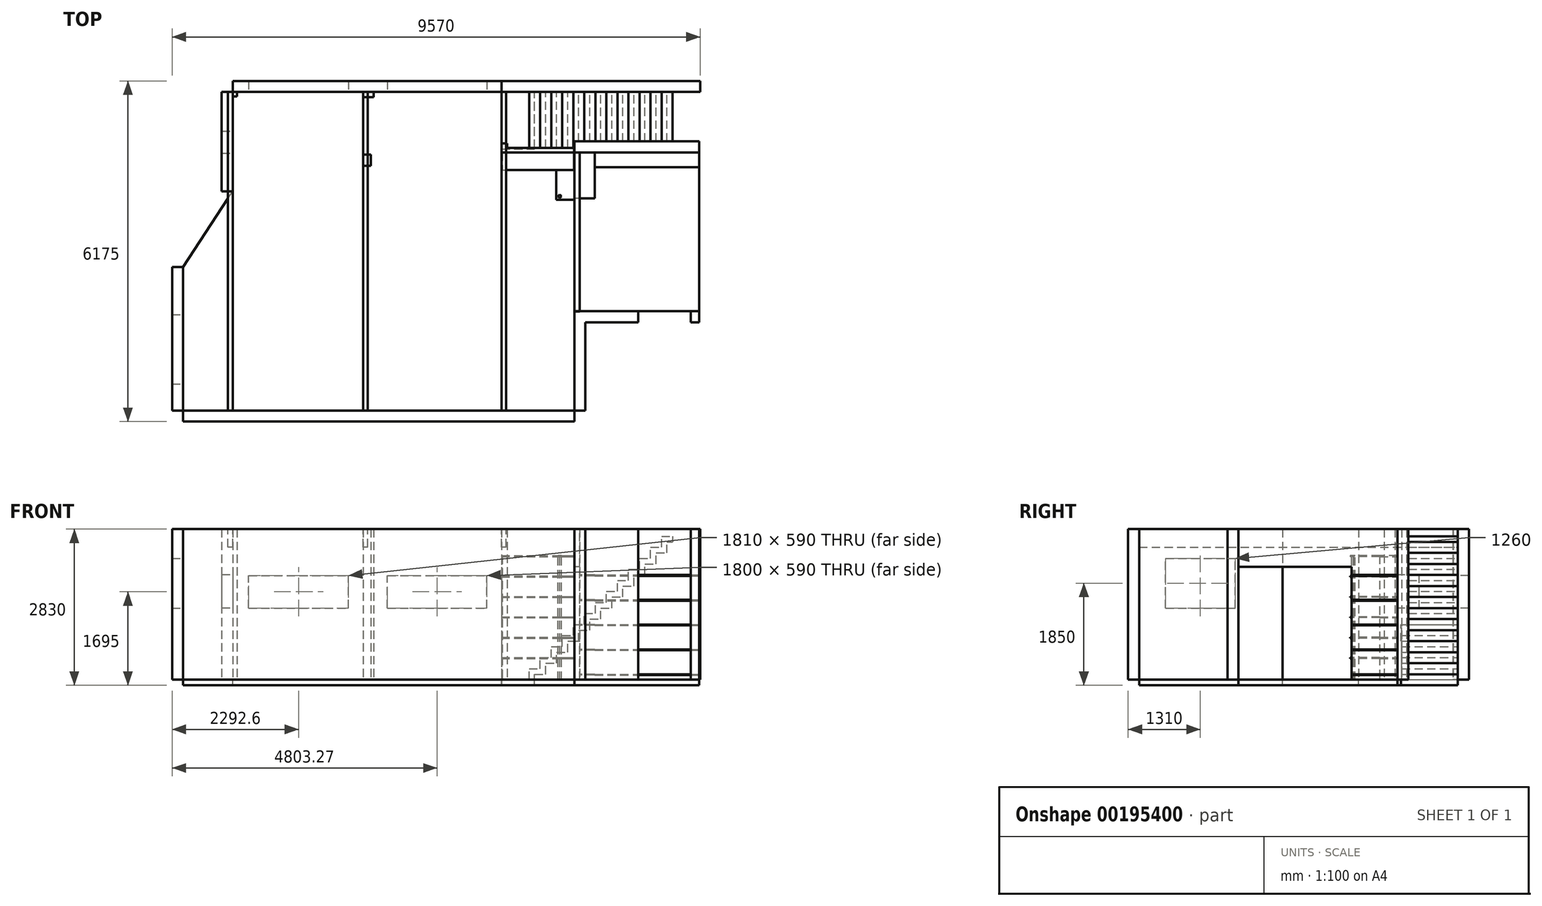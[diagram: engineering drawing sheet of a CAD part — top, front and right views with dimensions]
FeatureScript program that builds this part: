
annotation { "Feature Type Name" : "Feature", "Feature Type Description" : "" }
export const myFeature = defineFeature(function(context is Context, id is Id, definition is map)
    precondition{}
    {
        {
            var Q0;
            Q0=qCreatedBy(makeId("Top.planeOp"),FACE);
            var sketch = newSketch(context, id + "F0", { "sketchPlane" : qUnion([Q0])});
            skLineSegment(sketch, "E0.bottom", {"start": v(0, 0) * mm, "end": v(7090, 0) * mm});
            skLineSegment(sketch, "E0.top", {"start": v(0, 5775) * mm, "end": v(7090, 5775) * mm});
            skLineSegment(sketch, "E0.left", {"start": v(0, 0) * mm, "end": v(0, 5775) * mm});
            skLineSegment(sketch, "E0.right", {"start": v(7090, 0) * mm, "end": v(7090, 5775) * mm});
            skLineSegment(sketch, "E1", {"start": v(7090, 0) * mm, "end": v(7090, 1800) * mm, "construction": true});
            skLineSegment(sketch, "E2.bottom", {"start": v(7090, 1800) * mm, "end": v(9350, 1800) * mm});
            skLineSegment(sketch, "E2.top", {"start": v(7090, 4680) * mm, "end": v(9350, 4680) * mm});
            skLineSegment(sketch, "E2.left", {"start": v(7090, 1800) * mm, "end": v(7090, 4680) * mm});
            skLineSegment(sketch, "E2.right", {"start": v(9350, 1800) * mm, "end": v(9350, 4680) * mm});
            skLineSegment(sketch, "E3", {"start": v(7090, 4680) * mm, "end": v(7090, 3850) * mm, "construction": true});
            skLineSegment(sketch, "E4", {"start": v(0, 5775) * mm, "end": v(900, 5775) * mm, "construction": true});
            skLineSegment(sketch, "E5", {"start": v(900, 5775) * mm, "end": v(900, 3975) * mm, "construction": true});
            skLineSegment(sketch, "E6", {"start": v(0, 0) * mm, "end": v(0, 2600) * mm, "construction": true});
            skLineSegment(sketch, "E7", {"start": v(0, 2600) * mm, "end": v(900, 3975) * mm, "construction": true});
            skSolve(sketch);
        }
        {
            var Q0;
            Q0 = qSketchRegion(id + "F0", true);
            extrude(context, id + "F1", {"entities" : qUnion([Q0]), "oppositeDirection" : true, "depth" : 100 * mm});
        }
        {
            var Q0;
            Q0=makeQuery(id+"F1.opExtrude","CAP_FACE",FACE,{"disambiguationData":[OSD([sQuery(id+"F0.wireOp",EDGE,"E0.bottom"),sQuery(id+"F0.wireOp",EDGE,"E0.top"),sQuery(id+"F0.wireOp",EDGE,"E0.left"),sQuery(id+"F0.wireOp",EDGE,"E0.right"),sQuery(id+"F0.wireOp",EDGE,"E2.bottom"),sQuery(id+"F0.wireOp",EDGE,"E2.top"),sQuery(id+"F0.wireOp",EDGE,"E2.right")])],"isStart":true});
            var sketch = newSketch(context, id + "F2", { "sketchPlane" : qUnion([Q0])});
            skLineSegment(sketch, "E8", {"start": v(0, 5775) * mm, "end": v(900, 5775) * mm});
            skLineSegment(sketch, "E9", {"start": v(900, 5775) * mm, "end": v(900, 3975) * mm});
            skLineSegment(sketch, "E10", {"start": v(0, 2600) * mm, "end": v(900, 3975) * mm});
            skLineSegment(sketch, "E11", {"start": v(0, 5775) * mm, "end": v(0, 2600) * mm});
            skSolve(sketch);
        }
        {
            var Q0;
            Q0 = qSketchRegion(id + "F2", true);
            extrude(context, id + "F3", {"entities" : qUnion([Q0]), "operationType" : NewBodyOperationType.REMOVE, "endBound" : BoundingType.SYMMETRIC, "oppositeDirection" : true, "depth" : 210 * mm});
        }
        {
            var Q0;
            Q0=makeQuery(id+"F1.opExtrude","CAP_FACE",FACE,{"disambiguationData":[OSD([sQuery(id+"F0.wireOp",EDGE,"E0.bottom"),sQuery(id+"F0.wireOp",EDGE,"E0.top"),sQuery(id+"F0.wireOp",EDGE,"E0.left"),sQuery(id+"F0.wireOp",EDGE,"E0.right"),sQuery(id+"F0.wireOp",EDGE,"E2.bottom"),sQuery(id+"F0.wireOp",EDGE,"E2.top"),sQuery(id+"F0.wireOp",EDGE,"E2.right")])],"isStart":true});
            var sketch = newSketch(context, id + "F4", { "sketchPlane" : qUnion([Q0])});
            skLineSegment(sketch, "E12.bottom", {"start": v(0, 0) * mm, "end": v(-200, 0) * mm});
            skLineSegment(sketch, "E12.top", {"start": v(0, 2600) * mm, "end": v(-200, 2600) * mm});
            skLineSegment(sketch, "E12.left", {"start": v(0, 0) * mm, "end": v(0, 2600) * mm});
            skLineSegment(sketch, "E12.right", {"start": v(-200, 0) * mm, "end": v(-200, 2600) * mm});
            skLineSegment(sketch, "E13.bottom", {"start": v(900, 5775) * mm, "end": v(700, 5775) * mm});
            skLineSegment(sketch, "E13.top", {"start": v(900, 3975) * mm, "end": v(700, 3975) * mm});
            skLineSegment(sketch, "E13.left", {"start": v(900, 5775) * mm, "end": v(900, 3975) * mm});
            skLineSegment(sketch, "E13.right", {"start": v(700, 5775) * mm, "end": v(700, 3975) * mm});
            skLineSegment(sketch, "E14.bottom", {"start": v(900, 5775) * mm, "end": v(7090, 5775) * mm});
            skLineSegment(sketch, "E14.top", {"start": v(900, 5975) * mm, "end": v(7090, 5975) * mm});
            skLineSegment(sketch, "E14.left", {"start": v(900, 5775) * mm, "end": v(900, 5975) * mm});
            skLineSegment(sketch, "E14.right", {"start": v(7090, 5775) * mm, "end": v(7090, 5975) * mm});
            skLineSegment(sketch, "E15.bottom", {"start": v(0, 0) * mm, "end": v(7090, 0) * mm});
            skLineSegment(sketch, "E15.top", {"start": v(0, -200) * mm, "end": v(7090, -200) * mm});
            skLineSegment(sketch, "E15.left", {"start": v(0, 0) * mm, "end": v(0, -200) * mm});
            skLineSegment(sketch, "E15.right", {"start": v(7090, 0) * mm, "end": v(7090, -200) * mm});
            skLineSegment(sketch, "E16.bottom", {"start": v(7090, 0) * mm, "end": v(7290, 0) * mm});
            skLineSegment(sketch, "E16.top", {"start": v(7090, 1800) * mm, "end": v(7290, 1800) * mm});
            skLineSegment(sketch, "E16.left", {"start": v(7090, 0) * mm, "end": v(7090, 1800) * mm});
            skLineSegment(sketch, "E16.right", {"start": v(7290, 0) * mm, "end": v(7290, 1800) * mm});
            skLineSegment(sketch, "E17.bottom", {"start": v(7090, 1800) * mm, "end": v(8250, 1800) * mm});
            skLineSegment(sketch, "E17.top", {"start": v(7090, 1600) * mm, "end": v(8250, 1600) * mm});
            skLineSegment(sketch, "E17.left", {"start": v(7090, 1800) * mm, "end": v(7090, 1600) * mm});
            skLineSegment(sketch, "E17.right", {"start": v(8250, 1800) * mm, "end": v(8250, 1600) * mm});
            skLineSegment(sketch, "E18.bottom", {"start": v(9350, 1800) * mm, "end": v(9200, 1800) * mm});
            skLineSegment(sketch, "E18.top", {"start": v(9350, 1600) * mm, "end": v(9200, 1600) * mm});
            skLineSegment(sketch, "E18.left", {"start": v(9350, 1800) * mm, "end": v(9350, 1600) * mm});
            skLineSegment(sketch, "E18.right", {"start": v(9200, 1800) * mm, "end": v(9200, 1600) * mm});
            skLineSegment(sketch, "E19.bottom", {"start": v(7090, 4680) * mm, "end": v(9350, 4680) * mm});
            skLineSegment(sketch, "E19.top", {"start": v(7090, 4880) * mm, "end": v(9350, 4880) * mm});
            skLineSegment(sketch, "E19.left", {"start": v(7090, 4680) * mm, "end": v(7090, 4880) * mm});
            skLineSegment(sketch, "E19.right", {"start": v(9350, 4680) * mm, "end": v(9350, 4880) * mm});
            skSolve(sketch);
        }
        {
            var Q0;
            Q0 = qSketchRegion(id + "F4", true);
            extrude(context, id + "F5", {"entities" : qUnion([Q0]), "depth" : 2730 * mm});
        }
        {
            var Q0;
            Q0=makeQuery(id+"F5.opExtrude","SWEPT_FACE",FACE,{"disambiguationData":[OSD([sQuery(id+"F4.wireOp",EDGE,"E12.left")])]});
            var sketch = newSketch(context, id + "F6", { "sketchPlane" : qUnion([Q0])});
            skLineSegment(sketch, "E20", {"start": v(0, 0) * mm, "end": v(0, 1300) * mm, "construction": true});
            skLineSegment(sketch, "E21", {"start": v(0, 1300) * mm, "end": v(480, 1300) * mm, "construction": true});
            skLineSegment(sketch, "E22.bottom", {"start": v(480, 1300) * mm, "end": v(1740, 1300) * mm});
            skLineSegment(sketch, "E22.top", {"start": v(480, 2200) * mm, "end": v(1740, 2200) * mm});
            skLineSegment(sketch, "E22.left", {"start": v(480, 1300) * mm, "end": v(480, 2200) * mm});
            skLineSegment(sketch, "E22.right", {"start": v(1740, 1300) * mm, "end": v(1740, 2200) * mm});
            skSolve(sketch);
        }
        {
            var Q0;
            Q0 = qSketchRegion(id + "F6", true);
            extrude(context, id + "F7", {"entities" : qUnion([Q0]), "operationType" : NewBodyOperationType.REMOVE, "oppositeDirection" : true, "depth" : 210 * mm});
        }
        {
            var Q0;
            Q0=makeQuery(id+"F5.opExtrude","SWEPT_FACE",FACE,{"disambiguationData":[OSD([sQuery(id+"F4.wireOp",EDGE,"E13.left")])]});
            var sketch = newSketch(context, id + "F8", { "sketchPlane" : qUnion([Q0])});
            skLineSegment(sketch, "E23", {"start": v(4875, 0) * mm, "end": v(4875, 1305) * mm, "construction": true});
            skLineSegment(sketch, "E24.bottom", {"start": v(4668.89, 1904.93) * mm, "end": v(5068.89, 1904.93) * mm});
            skLineSegment(sketch, "E24.top", {"start": v(4668.89, 1304.93) * mm, "end": v(5068.89, 1304.93) * mm});
            skLineSegment(sketch, "E24.left", {"start": v(4668.89, 1904.93) * mm, "end": v(4668.89, 1304.93) * mm});
            skLineSegment(sketch, "E24.right", {"start": v(5068.89, 1904.93) * mm, "end": v(5068.89, 1304.93) * mm});
            skSolve(sketch);
        }
        {
            var Q0;
            Q0 = qSketchRegion(id + "F8", true);
            extrude(context, id + "F9", {"entities" : qUnion([Q0]), "operationType" : NewBodyOperationType.REMOVE, "oppositeDirection" : true, "depth" : 210 * mm});
        }
        {
            var Q0;
            Q0=makeQuery(id+"F1.opExtrude","CAP_FACE",FACE,{"disambiguationData":[OSD([sQuery(id+"F0.wireOp",EDGE,"E0.bottom"),sQuery(id+"F0.wireOp",EDGE,"E0.top"),sQuery(id+"F0.wireOp",EDGE,"E0.left"),sQuery(id+"F0.wireOp",EDGE,"E0.right"),sQuery(id+"F0.wireOp",EDGE,"E2.bottom"),sQuery(id+"F0.wireOp",EDGE,"E2.top"),sQuery(id+"F0.wireOp",EDGE,"E2.right")])],"isStart":true});
            var sketch = newSketch(context, id + "F10", { "sketchPlane" : qUnion([Q0])});
            skLineSegment(sketch, "E25.bottom", {"start": v(900, 5775) * mm, "end": v(980, 5775) * mm});
            skLineSegment(sketch, "E25.top", {"start": v(900, 5695) * mm, "end": v(980, 5695) * mm});
            skLineSegment(sketch, "E25.left", {"start": v(900, 5775) * mm, "end": v(900, 5695) * mm});
            skLineSegment(sketch, "E25.right", {"start": v(980, 5775) * mm, "end": v(980, 5695) * mm});
            skLineSegment(sketch, "E26", {"start": v(980, 5775) * mm, "end": v(3260, 5775) * mm, "construction": true});
            skLineSegment(sketch, "E27.bottom", {"start": v(3260, 5775) * mm, "end": v(3455, 5775) * mm});
            skLineSegment(sketch, "E27.top", {"start": v(3260, 5685) * mm, "end": v(3455, 5685) * mm});
            skLineSegment(sketch, "E27.left", {"start": v(3260, 5775) * mm, "end": v(3260, 5685) * mm});
            skLineSegment(sketch, "E27.right", {"start": v(3455, 5775) * mm, "end": v(3455, 5685) * mm});
            skLineSegment(sketch, "E28", {"start": v(3260, 5775) * mm, "end": v(3260, 4640) * mm, "construction": true});
            skLineSegment(sketch, "E29.bottom", {"start": v(3260, 4640) * mm, "end": v(3405, 4640) * mm});
            skLineSegment(sketch, "E29.top", {"start": v(3260, 4440) * mm, "end": v(3405, 4440) * mm});
            skLineSegment(sketch, "E29.left", {"start": v(3260, 4640) * mm, "end": v(3260, 4440) * mm});
            skLineSegment(sketch, "E29.right", {"start": v(3405, 4640) * mm, "end": v(3405, 4440) * mm});
            skLineSegment(sketch, "E30", {"start": v(7090, 4680) * mm, "end": v(7090, 4800) * mm, "construction": true});
            skLineSegment(sketch, "E31", {"start": v(900, 3975) * mm, "end": v(0, 2600) * mm, "construction": true});
            skSolve(sketch);
        }
        {
            var Q0;
            Q0 = qSketchRegion(id + "F10", true);
            extrude(context, id + "F11", {"entities" : qUnion([Q0]), "depth" : 2730 * mm});
        }
        {
            var Q0;
            Q0=makeQuery(id+"F5.opExtrude","SWEPT_FACE",FACE,{"disambiguationData":[OSD([sQuery(id+"F4.wireOp",EDGE,"E14.bottom")])]});
            var sketch = newSketch(context, id + "F12", { "sketchPlane" : qUnion([Q0])});
            skLineSegment(sketch, "E32", {"start": v(977.6, 0) * mm, "end": v(1187.6, 0) * mm, "construction": true});
            skLineSegment(sketch, "E33", {"start": v(1187.6, 0) * mm, "end": v(1187.6, 1300) * mm, "construction": true});
            skLineSegment(sketch, "E34.bottom", {"start": v(1187.6, 1300) * mm, "end": v(2997.6, 1300) * mm});
            skLineSegment(sketch, "E34.top", {"start": v(1187.6, 1890) * mm, "end": v(2997.6, 1890) * mm});
            skLineSegment(sketch, "E34.left", {"start": v(1187.6, 1300) * mm, "end": v(1187.6, 1890) * mm});
            skLineSegment(sketch, "E34.right", {"start": v(2997.6, 1300) * mm, "end": v(2997.6, 1890) * mm});
            skLineSegment(sketch, "E35", {"start": v(3458.27, 0) * mm, "end": v(3703.27, 0) * mm, "construction": true});
            skLineSegment(sketch, "E36", {"start": v(3703.27, 0) * mm, "end": v(3703.27, 1300) * mm, "construction": true});
            skLineSegment(sketch, "E37.bottom", {"start": v(3703.27, 1300) * mm, "end": v(5503.27, 1300) * mm});
            skLineSegment(sketch, "E37.top", {"start": v(3703.27, 1890) * mm, "end": v(5503.27, 1890) * mm});
            skLineSegment(sketch, "E37.left", {"start": v(3703.27, 1300) * mm, "end": v(3703.27, 1890) * mm});
            skLineSegment(sketch, "E37.right", {"start": v(5503.27, 1300) * mm, "end": v(5503.27, 1890) * mm});
            skSolve(sketch);
        }
        {
            var Q0;
            Q0 = qSketchRegion(id + "F12", true);
            extrude(context, id + "F13", {"entities" : qUnion([Q0]), "operationType" : NewBodyOperationType.REMOVE, "oppositeDirection" : true, "depth" : 210 * mm});
        }
        {
            var Q0;
            Q0=makeQuery(id+"F5.opExtrude","SWEPT_FACE",FACE,{"disambiguationData":[OSD([sQuery(id+"F4.wireOp",EDGE,"E19.left")])]});
            var sketch = newSketch(context, id + "F14", { "sketchPlane" : qUnion([Q0])});
            skLineSegment(sketch, "E38", {"start": v(-4680, 0) * mm, "end": v(-3850, 0) * mm});
            skLineSegment(sketch, "E39", {"start": v(-3850, 0) * mm, "end": v(-3850, 2050) * mm});
            skLineSegment(sketch, "E40", {"start": v(-3850, 2050) * mm, "end": v(-1794.24, 2050) * mm});
            skLineSegment(sketch, "E41", {"start": v(-1794.24, 2050) * mm, "end": v(-1794.24, 2730) * mm});
            skLineSegment(sketch, "E42", {"start": v(-1794.24, 2730) * mm, "end": v(-4680, 2730) * mm});
            skLineSegment(sketch, "E43", {"start": v(-4680, 2730) * mm, "end": v(-4680, 0) * mm});
            skSolve(sketch);
        }
        {
            var Q0;
            Q0 = qSketchRegion(id + "F14", true);
            extrude(context, id + "F15", {"entities" : qUnion([Q0]), "oppositeDirection" : true, "depth" : 100 * mm});
        }
        {
            var Q0;
            Q0=makeQuery(id+"F1.opExtrude","CAP_FACE",FACE,{"disambiguationData":[OSD([sQuery(id+"F0.wireOp",EDGE,"E0.bottom"),sQuery(id+"F0.wireOp",EDGE,"E0.top"),sQuery(id+"F0.wireOp",EDGE,"E0.left"),sQuery(id+"F0.wireOp",EDGE,"E0.right"),sQuery(id+"F0.wireOp",EDGE,"E2.bottom"),sQuery(id+"F0.wireOp",EDGE,"E2.top"),sQuery(id+"F0.wireOp",EDGE,"E2.right")])],"isStart":true});
            var sketch = newSketch(context, id + "F16", { "sketchPlane" : qUnion([Q0])});
            skLineSegment(sketch, "E44", {"start": v(7090, 4680) * mm, "end": v(5770, 4680) * mm});
            skLineSegment(sketch, "E45", {"start": v(5770, 4680) * mm, "end": v(5770, 5967.05) * mm});
            skLineSegment(sketch, "E46", {"start": v(5770, 5967.05) * mm, "end": v(7090, 5967.05) * mm});
            skLineSegment(sketch, "E47", {"start": v(7090, 5967.05) * mm, "end": v(7090, 4680) * mm});
            skSolve(sketch);
        }
        {
            var Q0;
            Q0 = qSketchRegion(id + "F16", true);
            extrude(context, id + "F17", {"entities" : qUnion([Q0]), "operationType" : NewBodyOperationType.REMOVE, "oppositeDirection" : true, "depth" : 260 * mm});
        }
        {
            var Q0;
            Q0=makeQuery(id+"F5.opExtrude","CAP_FACE",FACE,{"disambiguationData":[OSD([sQuery(id+"F4.wireOp",EDGE,"E14.bottom"),sQuery(id+"F4.wireOp",EDGE,"E14.top"),sQuery(id+"F4.wireOp",EDGE,"E14.left"),sQuery(id+"F4.wireOp",EDGE,"E14.right")])],"isStart":true});
            var sketch = newSketch(context, id + "F18", { "sketchPlane" : qUnion([Q0])});
            skLineSegment(sketch, "E48.bottom", {"start": v(7090, -5775) * mm, "end": v(5771.05, -5775) * mm});
            skLineSegment(sketch, "E48.top", {"start": v(7090, -5975) * mm, "end": v(5771.05, -5975) * mm});
            skLineSegment(sketch, "E48.left", {"start": v(7090, -5775) * mm, "end": v(7090, -5975) * mm});
            skLineSegment(sketch, "E48.right", {"start": v(5771.05, -5775) * mm, "end": v(5771.05, -5975) * mm});
            skSolve(sketch);
        }
        {
            var Q0;
            Q0 = qSketchRegion(id + "F18", true);
            extrude(context, id + "F19", {"entities" : qUnion([Q0]), "operationType" : NewBodyOperationType.REMOVE, "oppositeDirection" : true, "depth" : 3080 * mm});
        }
        {
            var Q0;
            Q0=makeQuery(id+"F1.opExtrude","CAP_FACE",FACE,{"disambiguationData":[OSD([sQuery(id+"F0.wireOp",EDGE,"E0.bottom"),sQuery(id+"F0.wireOp",EDGE,"E0.top"),sQuery(id+"F0.wireOp",EDGE,"E0.left"),sQuery(id+"F0.wireOp",EDGE,"E0.right"),sQuery(id+"F0.wireOp",EDGE,"E2.bottom"),sQuery(id+"F0.wireOp",EDGE,"E2.top"),sQuery(id+"F0.wireOp",EDGE,"E2.right")])],"isStart":true});
            var sketch = newSketch(context, id + "F20", { "sketchPlane" : qUnion([Q0])});
            skLineSegment(sketch, "E49", {"start": v(5770, 5775) * mm, "end": v(5770, 5745) * mm, "construction": true});
            skLineSegment(sketch, "E50", {"start": v(5770, 5745) * mm, "end": v(5770, 4845) * mm, "construction": true});
            skLineSegment(sketch, "E51", {"start": v(5770, 4845) * mm, "end": v(5770, 4680) * mm, "construction": true});
            skLineSegment(sketch, "E52", {"start": v(5770, 4845) * mm, "end": v(5870, 4845) * mm});
            skLineSegment(sketch, "E53", {"start": v(5870, 4845) * mm, "end": v(5870, 4761.18) * mm});
            skLineSegment(sketch, "E54", {"start": v(5870, 4761.18) * mm, "end": v(7088.39, 4761.18) * mm});
            skLineSegment(sketch, "E55", {"start": v(7088.39, 4761.18) * mm, "end": v(7088.39, 4680) * mm});
            skLineSegment(sketch, "E56", {"start": v(7088.39, 4680) * mm, "end": v(5770, 4680) * mm});
            skLineSegment(sketch, "E57", {"start": v(5770, 4680) * mm, "end": v(5770, 4845) * mm});
            skSolve(sketch);
        }
        {
            var Q0;
            Q0 = qSketchRegion(id + "F20", true);
            extrude(context, id + "F21", {"entities" : qUnion([Q0]), "depth" : 2730 * mm});
        }
        {
            var Q0;
            Q0=makeQuery(id+"F5.opExtrude","SWEPT_FACE",FACE,{"disambiguationData":[OSD([sQuery(id+"F4.wireOp",EDGE,"E14.bottom")])]});
            var sketch = newSketch(context, id + "F22", { "sketchPlane" : qUnion([Q0])});
            skLineSegment(sketch, "E58", {"start": v(5771.05, 0) * mm, "end": v(6271.05, 0) * mm});
            skLineSegment(sketch, "E59", {"start": v(6271.05, 0) * mm, "end": v(6271.05, 200) * mm});
            skLineSegment(sketch, "E60", {"start": v(6271.05, 200) * mm, "end": v(6471.05, 200) * mm});
            skLineSegment(sketch, "E61", {"start": v(6471.05, 200) * mm, "end": v(6471.05, 400) * mm});
            skLineSegment(sketch, "E62", {"start": v(6471.05, 400) * mm, "end": v(6671.05, 400) * mm});
            skLineSegment(sketch, "E63", {"start": v(6671.05, 400) * mm, "end": v(6671.05, 600) * mm});
            skLineSegment(sketch, "E64", {"start": v(6671.05, 600) * mm, "end": v(6871.05, 600) * mm});
            skLineSegment(sketch, "E65", {"start": v(6871.05, 600) * mm, "end": v(6871.05, 800) * mm});
            skLineSegment(sketch, "E66", {"start": v(6871.05, 800) * mm, "end": v(7071.05, 800) * mm});
            skLineSegment(sketch, "E67", {"start": v(7071.05, 800) * mm, "end": v(7071.05, 1000) * mm});
            skLineSegment(sketch, "E68", {"start": v(7071.05, 1000) * mm, "end": v(7271.05, 1000) * mm});
            skLineSegment(sketch, "E69", {"start": v(7271.05, 1000) * mm, "end": v(7271.05, 1200) * mm});
            skLineSegment(sketch, "E70", {"start": v(7271.05, 1200) * mm, "end": v(7471.05, 1200) * mm});
            skLineSegment(sketch, "E71", {"start": v(7471.05, 1200) * mm, "end": v(7471.05, 1400) * mm});
            skLineSegment(sketch, "E72", {"start": v(7471.05, 1400) * mm, "end": v(7671.05, 1400) * mm});
            skLineSegment(sketch, "E73", {"start": v(7671.05, 1400) * mm, "end": v(7671.05, 1600) * mm});
            skLineSegment(sketch, "E74", {"start": v(7671.05, 1600) * mm, "end": v(7871.05, 1600) * mm});
            skLineSegment(sketch, "E75", {"start": v(7871.05, 1600) * mm, "end": v(7871.05, 1800) * mm});
            skLineSegment(sketch, "E76", {"start": v(7871.05, 1800) * mm, "end": v(8071.05, 1800) * mm});
            skLineSegment(sketch, "E77", {"start": v(8071.05, 1800) * mm, "end": v(8071.05, 2000) * mm});
            skLineSegment(sketch, "E78", {"start": v(8071.05, 2000) * mm, "end": v(8271.05, 2000) * mm});
            skLineSegment(sketch, "E79", {"start": v(8271.05, 2000) * mm, "end": v(8271.05, 2200) * mm});
            skLineSegment(sketch, "E80", {"start": v(8271.05, 2200) * mm, "end": v(8471.05, 2200) * mm});
            skLineSegment(sketch, "E81", {"start": v(8471.05, 2200) * mm, "end": v(8471.05, 2400) * mm});
            skLineSegment(sketch, "E82", {"start": v(8471.05, 2400) * mm, "end": v(8671.05, 2400) * mm});
            skLineSegment(sketch, "E83", {"start": v(8671.05, 2400) * mm, "end": v(8671.05, 2600) * mm});
            skLineSegment(sketch, "E84", {"start": v(8671.05, 2600) * mm, "end": v(8871.05, 2600) * mm});
            skLineSegment(sketch, "E85.0", {"start": v(8771.05, 2500) * mm, "end": v(8871.05, 2500) * mm});
            skLineSegment(sketch, "E85.1", {"start": v(8771.05, 2300) * mm, "end": v(8771.05, 2500) * mm});
            skLineSegment(sketch, "E85.2", {"start": v(8571.05, 2300) * mm, "end": v(8771.05, 2300) * mm});
            skLineSegment(sketch, "E85.3", {"start": v(8571.05, 2100) * mm, "end": v(8571.05, 2300) * mm});
            skLineSegment(sketch, "E85.4", {"start": v(8371.05, 2100) * mm, "end": v(8571.05, 2100) * mm});
            skLineSegment(sketch, "E85.5", {"start": v(7171.05, 700) * mm, "end": v(7171.05, 900) * mm});
            skLineSegment(sketch, "E85.6", {"start": v(6971.05, 700) * mm, "end": v(7171.05, 700) * mm});
            skLineSegment(sketch, "E85.7", {"start": v(6971.05, 500) * mm, "end": v(6971.05, 700) * mm});
            skLineSegment(sketch, "E85.8", {"start": v(6771.05, 500) * mm, "end": v(6971.05, 500) * mm});
            skLineSegment(sketch, "E85.9", {"start": v(6771.05, 300) * mm, "end": v(6771.05, 500) * mm});
            skLineSegment(sketch, "E85.10", {"start": v(6571.05, 300) * mm, "end": v(6771.05, 300) * mm});
            skLineSegment(sketch, "E85.11", {"start": v(5771.05, -100) * mm, "end": v(6371.05, -100) * mm});
            skLineSegment(sketch, "E85.12", {"start": v(6371.05, -100) * mm, "end": v(6371.05, 100) * mm});
            skLineSegment(sketch, "E85.13", {"start": v(6371.05, 100) * mm, "end": v(6571.05, 100) * mm});
            skLineSegment(sketch, "E85.14", {"start": v(6571.05, 100) * mm, "end": v(6571.05, 300) * mm});
            skLineSegment(sketch, "E85.15", {"start": v(7171.05, 900) * mm, "end": v(7371.05, 900) * mm});
            skLineSegment(sketch, "E85.16", {"start": v(7371.05, 900) * mm, "end": v(7371.05, 1100) * mm});
            skLineSegment(sketch, "E85.17", {"start": v(7371.05, 1100) * mm, "end": v(7571.05, 1100) * mm});
            skLineSegment(sketch, "E85.18", {"start": v(7571.05, 1100) * mm, "end": v(7571.05, 1300) * mm});
            skLineSegment(sketch, "E85.19", {"start": v(7571.05, 1300) * mm, "end": v(7771.05, 1300) * mm});
            skLineSegment(sketch, "E85.20", {"start": v(7771.05, 1300) * mm, "end": v(7771.05, 1500) * mm});
            skLineSegment(sketch, "E85.21", {"start": v(7771.05, 1500) * mm, "end": v(7971.05, 1500) * mm});
            skLineSegment(sketch, "E85.22", {"start": v(7971.05, 1500) * mm, "end": v(7971.05, 1700) * mm});
            skLineSegment(sketch, "E85.23", {"start": v(7971.05, 1700) * mm, "end": v(8171.05, 1700) * mm});
            skLineSegment(sketch, "E85.24", {"start": v(8171.05, 1700) * mm, "end": v(8171.05, 1900) * mm});
            skLineSegment(sketch, "E85.25", {"start": v(8171.05, 1900) * mm, "end": v(8371.05, 1900) * mm});
            skLineSegment(sketch, "E85.26", {"start": v(8371.05, 1900) * mm, "end": v(8371.05, 2100) * mm});
            skLineSegment(sketch, "E86", {"start": v(8871.05, 2600) * mm, "end": v(8871.05, 2500) * mm});
            skLineSegment(sketch, "E87", {"start": v(5771.05, 0) * mm, "end": v(5771.05, -100) * mm});
            skSolve(sketch);
        }
        {
            var Q0;
            Q0 = qSketchRegion(id + "F22", true);
            extrude(context, id + "F23", {"entities" : qUnion([Q0]), "operationType" : NewBodyOperationType.ADD, "depth" : 1030 * mm});
        }
        {
            var Q0;
            Q0=makeQuery(id+"F1.opExtrude","CAP_FACE",FACE,{"disambiguationData":[OSD([sQuery(id+"F0.wireOp",EDGE,"E0.bottom"),sQuery(id+"F0.wireOp",EDGE,"E0.top"),sQuery(id+"F0.wireOp",EDGE,"E0.left"),sQuery(id+"F0.wireOp",EDGE,"E0.right"),sQuery(id+"F0.wireOp",EDGE,"E2.bottom"),sQuery(id+"F0.wireOp",EDGE,"E2.top"),sQuery(id+"F0.wireOp",EDGE,"E2.right")])],"isStart":true});
            var sketch = newSketch(context, id + "F24", { "sketchPlane" : qUnion([Q0])});
            skLineSegment(sketch, "E88.bottom", {"start": v(5770, 5775) * mm, "end": v(9370, 5775) * mm});
            skLineSegment(sketch, "E88.top", {"start": v(5770, 5975) * mm, "end": v(9370, 5975) * mm});
            skLineSegment(sketch, "E88.left", {"start": v(5770, 5775) * mm, "end": v(5770, 5975) * mm});
            skLineSegment(sketch, "E88.right", {"start": v(9370, 5775) * mm, "end": v(9370, 5975) * mm});
            skSolve(sketch);
        }
        {
            var Q0;
            Q0 = qSketchRegion(id + "F24", true);
            extrude(context, id + "F25", {"entities" : qUnion([Q0]), "depth" : 2730 * mm});
        }
        {
            var Q0;
            Q0=makeQuery(id+"F21.opExtrude","SWEPT_FACE",FACE,{"disambiguationData":[OSD([sQuery(id+"F20.wireOp",EDGE,"E56")])]});
            var sketch = newSketch(context, id + "F26", { "sketchPlane" : qUnion([Q0])});
            skLineSegment(sketch, "E89", {"start": v(5770, 0) * mm, "end": v(5770, 2250) * mm, "construction": true});
            skLineSegment(sketch, "E90", {"start": v(5770, 2250) * mm, "end": v(5770, 1880) * mm, "construction": true});
            skLineSegment(sketch, "E91", {"start": v(5770, 1880) * mm, "end": v(5770, 1510) * mm, "construction": true});
            skLineSegment(sketch, "E92", {"start": v(5770, 1510) * mm, "end": v(5770, 1140) * mm, "construction": true});
            skLineSegment(sketch, "E93", {"start": v(5770, 1140) * mm, "end": v(5770, 770) * mm, "construction": true});
            skLineSegment(sketch, "E94", {"start": v(5770, 770) * mm, "end": v(5770, 400) * mm, "construction": true});
            skLineSegment(sketch, "E95.bottom", {"start": v(5770, 2250) * mm, "end": v(7088.39, 2250) * mm});
            skLineSegment(sketch, "E95.top", {"start": v(5770, 2234) * mm, "end": v(7088.39, 2234) * mm});
            skLineSegment(sketch, "E95.left", {"start": v(5770, 2250) * mm, "end": v(5770, 2234) * mm});
            skLineSegment(sketch, "E95.right", {"start": v(7088.39, 2250) * mm, "end": v(7088.39, 2234) * mm});
            skLineSegment(sketch, "E96.bottom", {"start": v(5770, 1880) * mm, "end": v(7088.39, 1880) * mm});
            skLineSegment(sketch, "E96.top", {"start": v(5770, 1864) * mm, "end": v(7088.39, 1864) * mm});
            skLineSegment(sketch, "E96.left", {"start": v(5770, 1880) * mm, "end": v(5770, 1864) * mm});
            skLineSegment(sketch, "E96.right", {"start": v(7088.39, 1880) * mm, "end": v(7088.39, 1864) * mm});
            skLineSegment(sketch, "E97.bottom", {"start": v(5770, 1510) * mm, "end": v(7088.39, 1510) * mm});
            skLineSegment(sketch, "E97.top", {"start": v(5770, 1494) * mm, "end": v(7088.39, 1494) * mm});
            skLineSegment(sketch, "E97.left", {"start": v(5770, 1510) * mm, "end": v(5770, 1494) * mm});
            skLineSegment(sketch, "E97.right", {"start": v(7088.39, 1510) * mm, "end": v(7088.39, 1494) * mm});
            skLineSegment(sketch, "E98.bottom", {"start": v(5770, 1140) * mm, "end": v(7088.39, 1140) * mm});
            skLineSegment(sketch, "E98.top", {"start": v(5770, 1124) * mm, "end": v(7088.39, 1124) * mm});
            skLineSegment(sketch, "E98.left", {"start": v(5770, 1140) * mm, "end": v(5770, 1124) * mm});
            skLineSegment(sketch, "E98.right", {"start": v(7088.39, 1140) * mm, "end": v(7088.39, 1124) * mm});
            skLineSegment(sketch, "E99.bottom", {"start": v(5770, 770) * mm, "end": v(7088.39, 770) * mm});
            skLineSegment(sketch, "E99.top", {"start": v(5770, 754) * mm, "end": v(7088.39, 754) * mm});
            skLineSegment(sketch, "E99.left", {"start": v(5770, 770) * mm, "end": v(5770, 754) * mm});
            skLineSegment(sketch, "E99.right", {"start": v(7088.39, 770) * mm, "end": v(7088.39, 754) * mm});
            skLineSegment(sketch, "E100.bottom", {"start": v(5770, 400) * mm, "end": v(7088.39, 400) * mm});
            skLineSegment(sketch, "E100.top", {"start": v(5770, 384) * mm, "end": v(7088.39, 384) * mm});
            skLineSegment(sketch, "E100.left", {"start": v(5770, 400) * mm, "end": v(5770, 384) * mm});
            skLineSegment(sketch, "E100.right", {"start": v(7088.39, 400) * mm, "end": v(7088.39, 384) * mm});
            skSolve(sketch);
        }
        {
            var Q0;
            Q0 = qSketchRegion(id + "F26", true);
            extrude(context, id + "F27", {"entities" : qUnion([Q0]), "operationType" : NewBodyOperationType.ADD, "depth" : 320 * mm});
        }
        {
            var Q0;
            Q0=makeQuery(id+"F1.opExtrude","CAP_FACE",FACE,{"disambiguationData":[OSD([sQuery(id+"F0.wireOp",EDGE,"E0.bottom"),sQuery(id+"F0.wireOp",EDGE,"E0.top"),sQuery(id+"F0.wireOp",EDGE,"E0.left"),sQuery(id+"F0.wireOp",EDGE,"E0.right"),sQuery(id+"F0.wireOp",EDGE,"E2.bottom"),sQuery(id+"F0.wireOp",EDGE,"E2.top"),sQuery(id+"F0.wireOp",EDGE,"E2.right")])],"isStart":true});
            var sketch = newSketch(context, id + "F28", { "sketchPlane" : qUnion([Q0])});
            skLineSegment(sketch, "E101.bottom", {"start": v(5770, 4680) * mm, "end": v(5786, 4680) * mm});
            skLineSegment(sketch, "E101.top", {"start": v(5770, 4360) * mm, "end": v(5786, 4360) * mm});
            skLineSegment(sketch, "E101.left", {"start": v(5770, 4680) * mm, "end": v(5770, 4360) * mm});
            skLineSegment(sketch, "E101.right", {"start": v(5786, 4680) * mm, "end": v(5786, 4360) * mm});
            skSolve(sketch);
        }
        {
            var Q0;
            Q0 = qSketchRegion(id + "F28", true);
            extrude(context, id + "F29", {"entities" : qUnion([Q0]), "depth" : 2250 * mm});
        }
        {
            var Q0;
            Q0=makeQuery(id+"F15.opExtrude","SWEPT_FACE",FACE,{"disambiguationData":[OSD([sQuery(id+"F14.wireOp",EDGE,"E39")])]});
            cPlane(context, id + "F30", {"entities" : qUnion([Q0]), "cplaneType" : CPlaneType.OFFSET, "offset" : 25 * mm, "width" : 150 * mm, "height" : 150 * mm});
        }
        {
            var Q0;
            Q0=qCreatedBy(id+"F30.planeOp",FACE);
            var sketch = newSketch(context, id + "F31", { "sketchPlane" : qUnion([Q0])});
            skLineSegment(sketch, "E102", {"start": v(0, 0) * mm, "end": v(7090, 0) * mm, "construction": true});
            skLineSegment(sketch, "E103", {"start": v(7090, 0) * mm, "end": v(7090, 2250) * mm, "construction": true});
            skLineSegment(sketch, "E104", {"start": v(7090, 2250) * mm, "end": v(7090, 1880) * mm, "construction": true});
            skLineSegment(sketch, "E105", {"start": v(7090, 1880) * mm, "end": v(7090, 1510) * mm, "construction": true});
            skLineSegment(sketch, "E106", {"start": v(7090, 1510) * mm, "end": v(7090, 1140) * mm, "construction": true});
            skLineSegment(sketch, "E107", {"start": v(7090, 1140) * mm, "end": v(7090, 770) * mm, "construction": true});
            skLineSegment(sketch, "E108", {"start": v(7090, 770) * mm, "end": v(7090, 400) * mm, "construction": true});
            skLineSegment(sketch, "E109.bottom", {"start": v(7090, 2250) * mm, "end": v(6765, 2250) * mm});
            skLineSegment(sketch, "E109.top", {"start": v(7090, 2234) * mm, "end": v(6765, 2234) * mm});
            skLineSegment(sketch, "E109.left", {"start": v(7090, 2250) * mm, "end": v(7090, 2234) * mm});
            skLineSegment(sketch, "E109.right", {"start": v(6765, 2250) * mm, "end": v(6765, 2234) * mm});
            skLineSegment(sketch, "E110.bottom", {"start": v(7090, 1880) * mm, "end": v(6765, 1880) * mm});
            skLineSegment(sketch, "E110.top", {"start": v(7090, 1864) * mm, "end": v(6765, 1864) * mm});
            skLineSegment(sketch, "E110.left", {"start": v(7090, 1880) * mm, "end": v(7090, 1864) * mm});
            skLineSegment(sketch, "E110.right", {"start": v(6765, 1880) * mm, "end": v(6765, 1864) * mm});
            skLineSegment(sketch, "E111.bottom", {"start": v(7090, 1510) * mm, "end": v(6765, 1510) * mm});
            skLineSegment(sketch, "E111.top", {"start": v(7090, 1494) * mm, "end": v(6765, 1494) * mm});
            skLineSegment(sketch, "E111.left", {"start": v(7090, 1510) * mm, "end": v(7090, 1494) * mm});
            skLineSegment(sketch, "E111.right", {"start": v(6765, 1510) * mm, "end": v(6765, 1494) * mm});
            skLineSegment(sketch, "E112.bottom", {"start": v(7090, 1140) * mm, "end": v(6765, 1140) * mm});
            skLineSegment(sketch, "E112.top", {"start": v(7090, 1124) * mm, "end": v(6765, 1124) * mm});
            skLineSegment(sketch, "E112.left", {"start": v(7090, 1140) * mm, "end": v(7090, 1124) * mm});
            skLineSegment(sketch, "E112.right", {"start": v(6765, 1140) * mm, "end": v(6765, 1124) * mm});
            skLineSegment(sketch, "E113.bottom", {"start": v(7090, 770) * mm, "end": v(6765, 770) * mm});
            skLineSegment(sketch, "E113.top", {"start": v(7090, 754) * mm, "end": v(6765, 754) * mm});
            skLineSegment(sketch, "E113.left", {"start": v(7090, 770) * mm, "end": v(7090, 754) * mm});
            skLineSegment(sketch, "E113.right", {"start": v(6765, 770) * mm, "end": v(6765, 754) * mm});
            skLineSegment(sketch, "E114.bottom", {"start": v(7090, 400) * mm, "end": v(6765, 400) * mm});
            skLineSegment(sketch, "E114.top", {"start": v(7090, 384) * mm, "end": v(6765, 384) * mm});
            skLineSegment(sketch, "E114.left", {"start": v(7090, 400) * mm, "end": v(7090, 384) * mm});
            skLineSegment(sketch, "E114.right", {"start": v(6765, 400) * mm, "end": v(6765, 384) * mm});
            skSolve(sketch);
        }
        {
            var Q0;
            Q0 = qSketchRegion(id + "F31", true);
            var Q1;
            Q1=makeQuery(id+"F27.opExtrude","CAP_FACE",FACE,{"disambiguationData":[OSD([sQuery(id+"F26.wireOp",EDGE,"E96.bottom"),sQuery(id+"F26.wireOp",EDGE,"E96.top"),sQuery(id+"F26.wireOp",EDGE,"E96.left"),sQuery(id+"F26.wireOp",EDGE,"E96.right")])],"isStart":false});
            extrude(context, id + "F32", {"entities" : qUnion([Q0]), "endBound" : BoundingType.UP_TO_SURFACE, "oppositeDirection" : true, "endBoundEntityFace" : qUnion([Q1]), "depth" : 535.1 * mm});
        }
        {
            var Q0;
            Q0=makeQuery(id+"F32.opExtrude","SWEPT_FACE",FACE,{"disambiguationData":[OSD([sQuery(id+"F31.wireOp",EDGE,"E109.bottom")])]});
            var sketch = newSketch(context, id + "F33", { "sketchPlane" : qUnion([Q0])});
            skLineSegment(sketch, "E115", {"start": v(7090, 3894.47) * mm, "end": v(6820, 3894.47) * mm, "construction": true});
            skLineSegment(sketch, "E116", {"start": v(6793.82, 3882.98) * mm, "end": v(6826.94, 3852.51) * mm});
            skLineSegment(sketch, "E117", {"start": v(6826.94, 3852.51) * mm, "end": v(6857.4, 3885.63) * mm});
            skLineSegment(sketch, "E118", {"start": v(6857.4, 3885.63) * mm, "end": v(6824.3, 3916.1) * mm});
            skLineSegment(sketch, "E119", {"start": v(6824.3, 3916.1) * mm, "end": v(6793.82, 3882.98) * mm});
            skSolve(sketch);
        }
        {
            var Q0;
            Q0 = qSketchRegion(id + "F33", true);
            extrude(context, id + "F34", {"entities" : qUnion([Q0]), "oppositeDirection" : true, "depth" : 2250 * mm});
        }
        {
            var Q0;
            Q0=makeQuery(id+"F5.opExtrude","SWEPT_FACE",FACE,{"disambiguationData":[OSD([sQuery(id+"F4.wireOp",EDGE,"E13.top")])]});
            var sketch = newSketch(context, id + "F35", { "sketchPlane" : qUnion([Q0])});
            skSolve(sketch);
        }
        {
            var Q0;
            {var subQ0=sQuery(id+"F4.wireOp",EDGE,"E13.top");Q0=makeQuery(id+"F35.imprint","IMPRINT",FACE,{"disambiguationData":[TD([[makeQuery(id+"F35.imprint","IMPRINT",EDGE,{"derivedFrom":makeQuery(id+"F5.opExtrude","CAP_EDGE",EDGE,{"disambiguationData":[OSD([subQ0])],"isStart":true})}),-1.0]])]});}
            var sketch = newSketch(context, id + "F36", { "sketchPlane" : qUnion([Q0])});
            skLineSegment(sketch, "E120", {"start": v(900, 2730) * mm, "end": v(815, 2730) * mm, "construction": true});
            skLineSegment(sketch, "E121.bottom", {"start": v(815, 2730) * mm, "end": v(902, 2730) * mm});
            skLineSegment(sketch, "E121.top", {"start": v(815, 2405) * mm, "end": v(902, 2405) * mm});
            skLineSegment(sketch, "E121.left", {"start": v(815, 2730) * mm, "end": v(815, 2405) * mm});
            skLineSegment(sketch, "E121.right", {"start": v(902, 2730) * mm, "end": v(902, 2405) * mm});
            skLineSegment(sketch, "E122", {"start": v(902, 2730) * mm, "end": v(3260.06, 2730) * mm, "construction": true});
            skLineSegment(sketch, "E123.bottom", {"start": v(3260.06, 2730) * mm, "end": v(3345.06, 2730) * mm});
            skLineSegment(sketch, "E123.top", {"start": v(3260.06, 2405) * mm, "end": v(3345.06, 2405) * mm});
            skLineSegment(sketch, "E123.left", {"start": v(3260.06, 2730) * mm, "end": v(3260.06, 2405) * mm});
            skLineSegment(sketch, "E123.right", {"start": v(3345.06, 2730) * mm, "end": v(3345.06, 2405) * mm});
            skLineSegment(sketch, "E124", {"start": v(3345.06, 2730) * mm, "end": v(5768.81, 2730) * mm, "construction": true});
            skLineSegment(sketch, "E125.bottom", {"start": v(5768.81, 2730) * mm, "end": v(5853.81, 2730) * mm});
            skLineSegment(sketch, "E125.top", {"start": v(5768.81, 2405) * mm, "end": v(5853.81, 2405) * mm});
            skLineSegment(sketch, "E125.left", {"start": v(5768.81, 2730) * mm, "end": v(5768.81, 2405) * mm});
            skLineSegment(sketch, "E125.right", {"start": v(5853.81, 2730) * mm, "end": v(5853.81, 2405) * mm});
            skSolve(sketch);
        }
        {
            var Q0;
            Q0 = qSketchRegion(id + "F36", true);
            var Q1;
            Q1=makeQuery(id+"F5.opExtrude","SWEPT_FACE",FACE,{"disambiguationData":[OSD([sQuery(id+"F4.wireOp",EDGE,"E14.bottom")])]});
            extrude(context, id + "F37", {"entities" : qUnion([Q0]), "endBound" : BoundingType.UP_TO_NEXT, "depth" : 3975.2 * mm, "hasSecondDirection" : true, "secondDirectionBound" : SecondDirectionBoundingType.UP_TO_SURFACE, "secondDirectionOppositeDirection" : true, "secondDirectionBoundEntityFace" : qUnion([Q1]), "secondDirectionDepth" : 25 * mm});
        }
        {
            var Q0;
            Q0=makeQuery(id+"F15.opExtrude","CAP_FACE",FACE,{"disambiguationData":[OSD([sQuery(id+"F14.wireOp",EDGE,"E38"),sQuery(id+"F14.wireOp",EDGE,"E39"),sQuery(id+"F14.wireOp",EDGE,"E40"),sQuery(id+"F14.wireOp",EDGE,"E41"),sQuery(id+"F14.wireOp",EDGE,"E42"),sQuery(id+"F14.wireOp",EDGE,"E43")])],"isStart":false});
            var sketch = newSketch(context, id + "F38", { "sketchPlane" : qUnion([Q0])});
            skLineSegment(sketch, "E126", {"start": v(4680, 0) * mm, "end": v(4680, 1900) * mm, "construction": true});
            skLineSegment(sketch, "E127", {"start": v(4680, 1900) * mm, "end": v(4680, 1450) * mm, "construction": true});
            skLineSegment(sketch, "E128", {"start": v(4680, 1450) * mm, "end": v(4680, 1000) * mm, "construction": true});
            skLineSegment(sketch, "E129", {"start": v(4680, 1000) * mm, "end": v(4680, 550) * mm, "construction": true});
            skLineSegment(sketch, "E130", {"start": v(4680, 550) * mm, "end": v(4680, 100) * mm, "construction": true});
            skLineSegment(sketch, "E131.bottom", {"start": v(4680, 1900) * mm, "end": v(3850, 1900) * mm});
            skLineSegment(sketch, "E131.top", {"start": v(4680, 1884) * mm, "end": v(3850, 1884) * mm});
            skLineSegment(sketch, "E131.left", {"start": v(4680, 1900) * mm, "end": v(4680, 1884) * mm});
            skLineSegment(sketch, "E131.right", {"start": v(3850, 1900) * mm, "end": v(3850, 1884) * mm});
            skLineSegment(sketch, "E132.bottom", {"start": v(4680, 1450) * mm, "end": v(3850, 1450) * mm});
            skLineSegment(sketch, "E132.top", {"start": v(4680, 1434) * mm, "end": v(3850, 1434) * mm});
            skLineSegment(sketch, "E132.left", {"start": v(4680, 1450) * mm, "end": v(4680, 1434) * mm});
            skLineSegment(sketch, "E132.right", {"start": v(3850, 1450) * mm, "end": v(3850, 1434) * mm});
            skLineSegment(sketch, "E133.bottom", {"start": v(4680, 1000) * mm, "end": v(3850, 1000) * mm});
            skLineSegment(sketch, "E133.top", {"start": v(4680, 984) * mm, "end": v(3850, 984) * mm});
            skLineSegment(sketch, "E133.left", {"start": v(4680, 1000) * mm, "end": v(4680, 984) * mm});
            skLineSegment(sketch, "E133.right", {"start": v(3850, 1000) * mm, "end": v(3850, 984) * mm});
            skLineSegment(sketch, "E134.bottom", {"start": v(4680, 550) * mm, "end": v(3850, 550) * mm});
            skLineSegment(sketch, "E134.top", {"start": v(4680, 534) * mm, "end": v(3850, 534) * mm});
            skLineSegment(sketch, "E134.left", {"start": v(4680, 550) * mm, "end": v(4680, 534) * mm});
            skLineSegment(sketch, "E134.right", {"start": v(3850, 550) * mm, "end": v(3850, 534) * mm});
            skLineSegment(sketch, "E135.bottom", {"start": v(4680, 100) * mm, "end": v(3850, 100) * mm});
            skLineSegment(sketch, "E135.top", {"start": v(4680, 84) * mm, "end": v(3850, 84) * mm});
            skLineSegment(sketch, "E135.left", {"start": v(4680, 100) * mm, "end": v(4680, 84) * mm});
            skLineSegment(sketch, "E135.right", {"start": v(3850, 100) * mm, "end": v(3850, 84) * mm});
            skSolve(sketch);
        }
        {
            var Q0;
            Q0 = qSketchRegion(id + "F38", true);
            extrude(context, id + "F39", {"entities" : qUnion([Q0]), "depth" : 270 * mm});
        }
        {
            var Q0;
            Q0=makeQuery(id+"F5.opExtrude","SWEPT_FACE",FACE,{"disambiguationData":[OSD([sQuery(id+"F4.wireOp",EDGE,"E19.right")])]});
            var sketch = newSketch(context, id + "F40", { "sketchPlane" : qUnion([Q0])});
            skLineSegment(sketch, "E136", {"start": v(4680, 0) * mm, "end": v(4680, 1900) * mm, "construction": true});
            skLineSegment(sketch, "E137", {"start": v(4680, 1900) * mm, "end": v(4680, 1450) * mm, "construction": true});
            skLineSegment(sketch, "E138", {"start": v(4680, 1450) * mm, "end": v(4680, 1000) * mm, "construction": true});
            skLineSegment(sketch, "E139", {"start": v(4680, 1000) * mm, "end": v(4680, 550) * mm, "construction": true});
            skLineSegment(sketch, "E140", {"start": v(4680, 550) * mm, "end": v(4680, 100) * mm, "construction": true});
            skLineSegment(sketch, "E141.bottom", {"start": v(4680, 1900) * mm, "end": v(4410, 1900) * mm});
            skLineSegment(sketch, "E141.top", {"start": v(4680, 1884) * mm, "end": v(4410, 1884) * mm});
            skLineSegment(sketch, "E141.left", {"start": v(4680, 1900) * mm, "end": v(4680, 1884) * mm});
            skLineSegment(sketch, "E141.right", {"start": v(4410, 1900) * mm, "end": v(4410, 1884) * mm});
            skLineSegment(sketch, "E142.bottom", {"start": v(4680, 1450) * mm, "end": v(4410, 1450) * mm});
            skLineSegment(sketch, "E142.top", {"start": v(4680, 1434) * mm, "end": v(4410, 1434) * mm});
            skLineSegment(sketch, "E142.left", {"start": v(4680, 1450) * mm, "end": v(4680, 1434) * mm});
            skLineSegment(sketch, "E142.right", {"start": v(4410, 1450) * mm, "end": v(4410, 1434) * mm});
            skLineSegment(sketch, "E143.bottom", {"start": v(4680, 1000) * mm, "end": v(4410, 1000) * mm});
            skLineSegment(sketch, "E143.top", {"start": v(4680, 984) * mm, "end": v(4410, 984) * mm});
            skLineSegment(sketch, "E143.left", {"start": v(4680, 1000) * mm, "end": v(4680, 984) * mm});
            skLineSegment(sketch, "E143.right", {"start": v(4410, 1000) * mm, "end": v(4410, 984) * mm});
            skLineSegment(sketch, "E144.bottom", {"start": v(4680, 550) * mm, "end": v(4410, 550) * mm});
            skLineSegment(sketch, "E144.top", {"start": v(4680, 534) * mm, "end": v(4410, 534) * mm});
            skLineSegment(sketch, "E144.left", {"start": v(4680, 550) * mm, "end": v(4680, 534) * mm});
            skLineSegment(sketch, "E144.right", {"start": v(4410, 550) * mm, "end": v(4410, 534) * mm});
            skLineSegment(sketch, "E145.bottom", {"start": v(4680, 100) * mm, "end": v(4410, 100) * mm});
            skLineSegment(sketch, "E145.top", {"start": v(4680, 84) * mm, "end": v(4410, 84) * mm});
            skLineSegment(sketch, "E145.left", {"start": v(4680, 100) * mm, "end": v(4680, 84) * mm});
            skLineSegment(sketch, "E145.right", {"start": v(4410, 100) * mm, "end": v(4410, 84) * mm});
            skSolve(sketch);
        }
        {
            var Q0;
            Q0 = qSketchRegion(id + "F40", true);
            var Q1;
            Q1=makeQuery(id+"F39.opExtrude","CAP_FACE",FACE,{"disambiguationData":[OSD([sQuery(id+"F38.wireOp",EDGE,"E133.bottom"),sQuery(id+"F38.wireOp",EDGE,"E133.top"),sQuery(id+"F38.wireOp",EDGE,"E133.left"),sQuery(id+"F38.wireOp",EDGE,"E133.right")])],"isStart":false});
            extrude(context, id + "F41", {"entities" : qUnion([Q0]), "endBound" : BoundingType.UP_TO_SURFACE, "oppositeDirection" : true, "endBoundEntityFace" : qUnion([Q1]), "depth" : 25 * mm});
        }
    });
